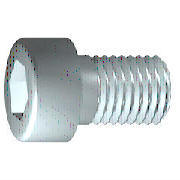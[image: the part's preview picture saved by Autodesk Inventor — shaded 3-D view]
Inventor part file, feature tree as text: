
AUTODESK INVENTOR PART (.ipt)
format: ipt  version: 2017.3 (Build 213256000, 256)  size: 193,024 bytes
history: native  units: mm (DEFAULTED — no unit token found)
features: sketch x2, extrude x1, plane x1, fillet x1
ambient origin geometry x7: Origin, YZ Plane, XY Plane, X Axis, Y Axis, Z Axis, Center Point
bodies: Solid1 (feature_tree), Body (feature_tree)
feature tree (5):
  extrude  "Slot"  Depth=3.0mm
  plane  "Work Plane1"
  fillet  "Fillet2"  Radius=3.0mm
  sketch  "Sketch1"  dims[d1=4.75mm d2=0.306825mm d3=3.0mm]
  sketch  "Sketch2"  dims[d4=1.3mm d5=60.0deg d6=3.0mm d7=3.0mm d8=2.886751mm d9=5.5mm d10=90.0deg d11=10.0mm d12=0.0mm d13=4.75mm d14=0.0mm d15=0.306725mm d16=0.306725mm d17=0.3mm d19=0.0mm d26=6.0mm d27=45.0deg d28=0.0mm d29=0.0mm d30=0.1mm]
